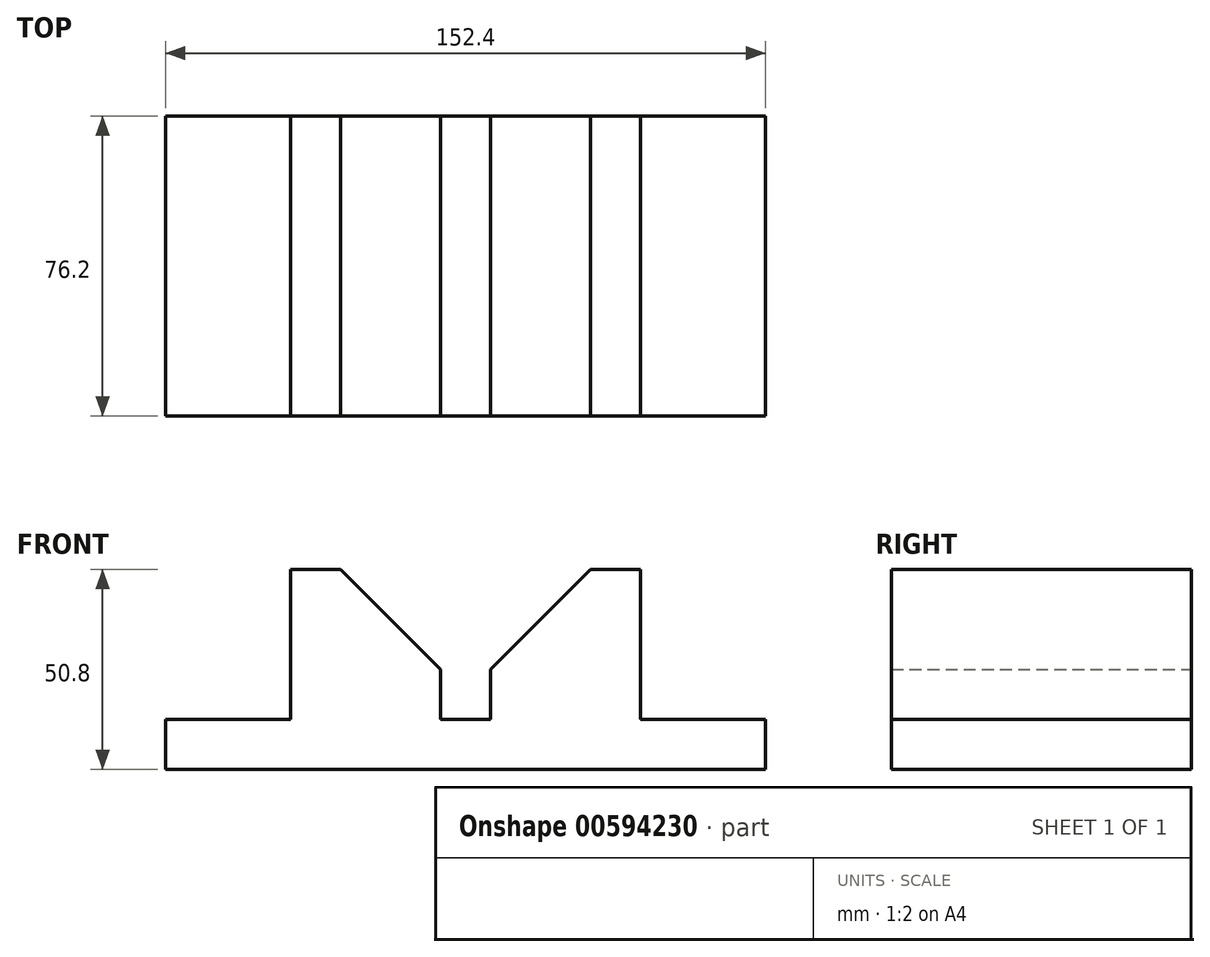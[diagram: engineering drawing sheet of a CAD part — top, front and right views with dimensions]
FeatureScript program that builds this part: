
annotation { "Feature Type Name" : "Feature", "Feature Type Description" : "" }
export const myFeature = defineFeature(function(context is Context, id is Id, definition is map)
    precondition{}
    {
        {
            var Q0;
            Q0=qCreatedBy(makeId("Front.planeOp"),FACE);
            var sketch = newSketch(context, id + "F0", { "sketchPlane" : qUnion([Q0])});
            skLineSegment(sketch, "E0", {"start": v(0, 0) * mm, "end": v(152.4, 0) * mm});
            skLineSegment(sketch, "E1", {"start": v(152.4, 0) * mm, "end": v(152.4, 12.7) * mm});
            skLineSegment(sketch, "E2", {"start": v(152.4, 12.7) * mm, "end": v(120.65, 12.7) * mm});
            skLineSegment(sketch, "E3", {"start": v(120.65, 12.7) * mm, "end": v(120.65, 50.8) * mm});
            skLineSegment(sketch, "E4", {"start": v(120.65, 50.8) * mm, "end": v(107.95, 50.8) * mm});
            skLineSegment(sketch, "E5", {"start": v(107.95, 50.8) * mm, "end": v(82.55, 25.4) * mm});
            skLineSegment(sketch, "E6", {"start": v(82.55, 25.4) * mm, "end": v(82.55, 12.7) * mm});
            skLineSegment(sketch, "E7", {"start": v(82.55, 12.7) * mm, "end": v(69.85, 12.7) * mm});
            skLineSegment(sketch, "E8", {"start": v(69.85, 12.7) * mm, "end": v(69.85, 25.4) * mm});
            skLineSegment(sketch, "E9", {"start": v(69.85, 25.4) * mm, "end": v(44.45, 50.8) * mm});
            skLineSegment(sketch, "E10", {"start": v(44.45, 50.8) * mm, "end": v(31.75, 50.8) * mm});
            skLineSegment(sketch, "E11", {"start": v(31.75, 50.8) * mm, "end": v(31.75, 12.7) * mm});
            skLineSegment(sketch, "E12", {"start": v(31.75, 12.7) * mm, "end": v(0, 12.7) * mm});
            skLineSegment(sketch, "E13", {"start": v(0, 12.7) * mm, "end": v(0, 0) * mm});
            skSolve(sketch);
        }
        {
            var Q0;
            Q0=makeQuery(id+"F0.imprint","IMPRINT",FACE,{"disambiguationData":[TD([[makeQuery(id+"F0.imprint","IMPRINT",EDGE,{"derivedFrom":sQuery(id+"F0.wireOp",EDGE,"E0")}),1.0]])]});
            extrude(context, id + "F1", {"entities" : qUnion([Q0]), "depth" : 76.2 * mm, "offsetDistance" : 25.4 * mm});
        }
    });
